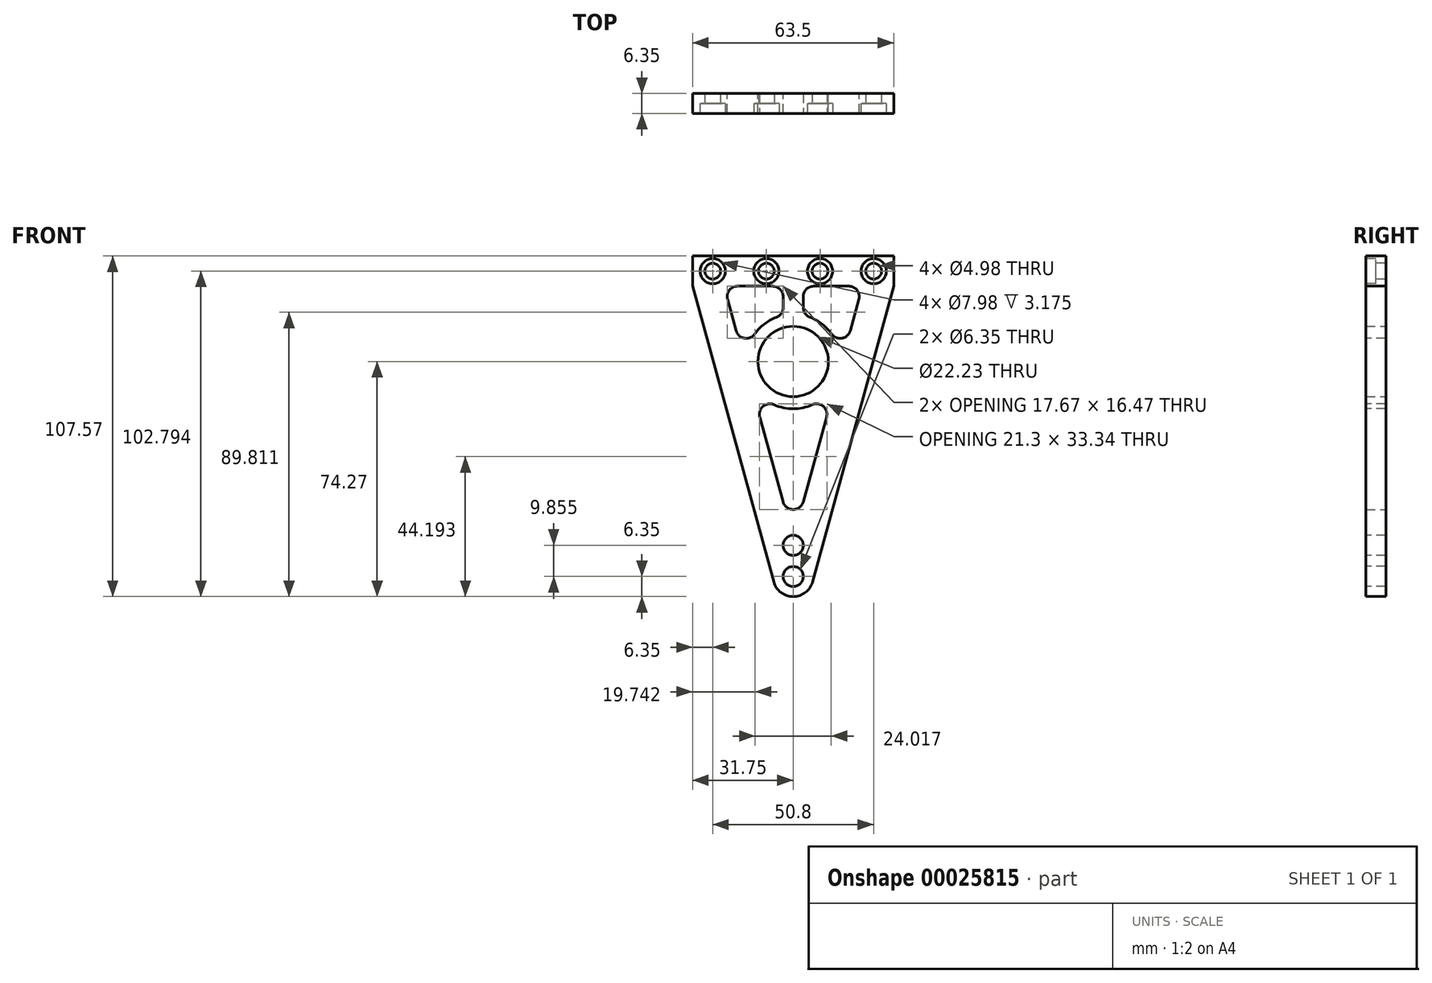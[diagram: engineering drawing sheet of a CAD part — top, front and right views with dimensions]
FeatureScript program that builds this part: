
annotation { "Feature Type Name" : "Feature", "Feature Type Description" : "" }
export const myFeature = defineFeature(function(context is Context, id is Id, definition is map)
    precondition{}
    {
        {
            var Q0;
            Q0=qCreatedBy(makeId("Front.planeOp"),FACE);
            var sketch = newSketch(context, id + "F0", { "sketchPlane" : qUnion([Q0])});
            skCircle(sketch, "E0", {"center": v(0, 0) * mm, "radius": 11.11 * mm});
            skLineSegment(sketch, "E1", {"start": v(0, 0) * mm, "end": v(0, 46.7) * mm, "construction": true});
            skLineSegment(sketch, "E2", {"start": v(0, 0) * mm, "end": v(31.75, 0) * mm, "construction": true});
            skLineSegment(sketch, "E3", {"start": v(-31.75, 33.3) * mm, "end": v(31.75, 33.3) * mm});
            skLineSegment(sketch, "E4", {"start": v(31.75, 33.3) * mm, "end": v(31.75, 23.77) * mm});
            skLineSegment(sketch, "E5", {"start": v(31.75, 23.77) * mm, "end": v(6.12, -69.6) * mm});
            skLineSegment(sketch, "E6", {"start": v(-6.12, -69.6) * mm, "end": v(-31.75, 23.77) * mm});
            skLineSegment(sketch, "E7", {"start": v(-31.75, 23.77) * mm, "end": v(-31.75, 33.3) * mm});
            skArc(sketch, "E8", {"start": v(-6.12, -69.6) * mm, "mid": v(0, -74.27) * mm, "end": v(6.12, -69.6) * mm});
            skSolve(sketch);
        }
        {
            var Q0;
            Q0=makeQuery(id+"F0.imprint","IMPRINT",FACE,{"disambiguationData":[TD([[makeQuery(id+"F0.imprint","IMPRINT",EDGE,{"derivedFrom":sQuery(id+"F0.wireOp",EDGE,"E0")}),-1.0]])]});
            extrude(context, id + "F1", {"entities" : qUnion([Q0]), "depth" : 6.35 * mm});
        }
        {
            var Q0;
            Q0=makeQuery(id+"F1.opExtrude","CAP_FACE",FACE,{"disambiguationData":[OSD([sQuery(id+"F0.wireOp",EDGE,"E0"),sQuery(id+"F0.wireOp",EDGE,"E3"),sQuery(id+"F0.wireOp",EDGE,"E4"),sQuery(id+"F0.wireOp",EDGE,"E5"),sQuery(id+"F0.wireOp",EDGE,"E6"),sQuery(id+"F0.wireOp",EDGE,"E7"),sQuery(id+"F0.wireOp",EDGE,"E8")])],"isStart":false});
            var sketch = newSketch(context, id + "F2", { "sketchPlane" : qUnion([Q0])});
            skLineSegment(sketch, "E9.0", {"start": v(21.87, 23.77) * mm, "end": v(3.17, 23.77) * mm});
            skLineSegment(sketch, "E9.1", {"start": v(0, -55.92) * mm, "end": v(13.77, -5.75) * mm});
            skLineSegment(sketch, "E9.2", {"start": v(-21.87, 23.77) * mm, "end": v(-14.78, -2.08) * mm});
            skArc(sketch, "E10", {"start": v(-13.77, -5.75) * mm, "mid": v(0, -14.92) * mm, "end": v(13.77, -5.75) * mm});
            skArc(sketch, "E11.trimOffspring", {"start": v(14.78, -2.08) * mm, "mid": v(12.25, 8.53) * mm, "end": v(3.18, 14.58) * mm});
            skLineSegment(sketch, "E12.trimOffspring", {"start": v(14.78, -2.08) * mm, "end": v(21.87, 23.77) * mm});
            skLineSegment(sketch, "E13.trimOffspring", {"start": v(-13.77, -5.75) * mm, "end": v(0, -55.92) * mm});
            skLineSegment(sketch, "E14", {"start": v(0, 0) * mm, "end": v(0, 36.66) * mm, "construction": true});
            skLineSegment(sketch, "E15", {"start": v(-3.17, 23.77) * mm, "end": v(-3.18, 14.58) * mm});
            skLineSegment(sketch, "E16", {"start": v(3.17, 23.77) * mm, "end": v(3.18, 14.58) * mm});
            skPoint(sketch, "E17.orphan", {"position": v(3.18, 0) * mm});
            skPoint(sketch, "E18.orphan", {"position": v(-3.18, 0) * mm});
            skArc(sketch, "E19.trimOffspring", {"start": v(-3.18, 14.58) * mm, "mid": v(-12.25, 8.53) * mm, "end": v(-14.78, -2.08) * mm});
            skLineSegment(sketch, "E20.trimOffspring", {"start": v(-3.17, 23.77) * mm, "end": v(-21.87, 23.77) * mm});
            skSolve(sketch);
        }
        {
            var Q0;
            Q0=makeQuery(id+"F2.imprint","IMPRINT",FACE,{"disambiguationData":[TD([[makeQuery(id+"F2.imprint","IMPRINT",EDGE,{"derivedFrom":sQuery(id+"F2.wireOp",EDGE,"E9.2")}),1.0]])]});
            var Q1;
            Q1=makeQuery(id+"F2.imprint","IMPRINT",FACE,{"disambiguationData":[TD([[makeQuery(id+"F2.imprint","IMPRINT",EDGE,{"derivedFrom":sQuery(id+"F2.wireOp",EDGE,"E9.0")}),1.0]])]});
            var Q2;
            Q2=makeQuery(id+"F2.imprint","IMPRINT",FACE,{"disambiguationData":[TD([[makeQuery(id+"F2.imprint","IMPRINT",EDGE,{"derivedFrom":sQuery(id+"F2.wireOp",EDGE,"E9.1")}),1.0]])]});
            extrude(context, id + "F3", {"entities" : qUnion([Q0, Q1, Q2]), "operationType" : NewBodyOperationType.REMOVE, "endBound" : BoundingType.THROUGH_ALL, "oppositeDirection" : true, "depth" : 25.4 * mm});
        }
        {
            var Q0;
            Q0=makeQuery(id+"F3.boolean.opBoolean","COPY",EDGE,{"derivedFrom":makeQuery(id+"F3.opExtrude","SWEPT_EDGE",EDGE,{"disambiguationData":[OSD([sQuery(id+"F2.wireOp",EDGE,"E9.0"),sQuery(id+"F2.wireOp",EDGE,"E12.trimOffspring")])]})});
            var Q1;
            Q1=makeQuery(id+"F3.boolean.opBoolean","COPY",EDGE,{"derivedFrom":makeQuery(id+"F3.opExtrude","SWEPT_EDGE",EDGE,{"disambiguationData":[OSD([sQuery(id+"F2.wireOp",EDGE,"E15"),sQuery(id+"F2.wireOp",EDGE,"E20.trimOffspring")])]})});
            var Q2;
            Q2=makeQuery(id+"F3.boolean.opBoolean","COPY",EDGE,{"derivedFrom":makeQuery(id+"F3.opExtrude","SWEPT_EDGE",EDGE,{"disambiguationData":[OSD([sQuery(id+"F2.wireOp",EDGE,"E9.0"),sQuery(id+"F2.wireOp",EDGE,"E16")])]})});
            var Q3;
            Q3=makeQuery(id+"F3.boolean.opBoolean","COPY",EDGE,{"derivedFrom":makeQuery(id+"F3.opExtrude","SWEPT_EDGE",EDGE,{"disambiguationData":[OSD([sQuery(id+"F2.wireOp",EDGE,"E9.2"),sQuery(id+"F2.wireOp",EDGE,"E20.trimOffspring")])]})});
            var Q4;
            Q4=makeQuery(id+"F3.boolean.opBoolean","COPY",EDGE,{"derivedFrom":makeQuery(id+"F3.opExtrude","SWEPT_EDGE",EDGE,{"disambiguationData":[OSD([sQuery(id+"F2.wireOp",EDGE,"E11.trimOffspring"),sQuery(id+"F2.wireOp",EDGE,"E12.trimOffspring")])]})});
            var Q5;
            Q5=makeQuery(id+"F3.boolean.opBoolean","COPY",EDGE,{"derivedFrom":makeQuery(id+"F3.opExtrude","SWEPT_EDGE",EDGE,{"disambiguationData":[OSD([sQuery(id+"F2.wireOp",EDGE,"E9.2"),sQuery(id+"F2.wireOp",EDGE,"E19.trimOffspring")])]})});
            var Q6;
            Q6=makeQuery(id+"F3.boolean.opBoolean","COPY",EDGE,{"derivedFrom":makeQuery(id+"F3.opExtrude","SWEPT_EDGE",EDGE,{"disambiguationData":[OSD([sQuery(id+"F2.wireOp",EDGE,"E9.1"),sQuery(id+"F2.wireOp",EDGE,"E13.trimOffspring")])]})});
            var Q7;
            Q7=makeQuery(id+"F3.boolean.opBoolean","COPY",EDGE,{"derivedFrom":makeQuery(id+"F3.opExtrude","SWEPT_EDGE",EDGE,{"disambiguationData":[OSD([sQuery(id+"F2.wireOp",EDGE,"E10"),sQuery(id+"F2.wireOp",EDGE,"E13.trimOffspring")])]})});
            var Q8;
            Q8=makeQuery(id+"F3.boolean.opBoolean","COPY",EDGE,{"derivedFrom":makeQuery(id+"F3.opExtrude","SWEPT_EDGE",EDGE,{"disambiguationData":[OSD([sQuery(id+"F2.wireOp",EDGE,"E9.1"),sQuery(id+"F2.wireOp",EDGE,"E10")])]})});
            var Q9;
            Q9=makeQuery(id+"F3.boolean.opBoolean","COPY",EDGE,{"derivedFrom":makeQuery(id+"F3.opExtrude","SWEPT_EDGE",EDGE,{"disambiguationData":[OSD([sQuery(id+"F2.wireOp",EDGE,"E11.trimOffspring"),sQuery(id+"F2.wireOp",EDGE,"E16")])]})});
            var Q10;
            Q10=makeQuery(id+"F3.boolean.opBoolean","COPY",EDGE,{"derivedFrom":makeQuery(id+"F3.opExtrude","SWEPT_EDGE",EDGE,{"disambiguationData":[OSD([sQuery(id+"F2.wireOp",EDGE,"E15"),sQuery(id+"F2.wireOp",EDGE,"E19.trimOffspring")])]})});
            fillet(context, id + "F4", {"entities" : qUnion([Q0, Q1, Q2, Q3, Q4, Q5, Q6, Q7, Q8, Q9, Q10]), "radius" : 3.3 * mm, "tangentPropagation" : true, "allowEdgeOverflow" : false});
        }
        {
            var Q0;
            Q0=makeQuery(id+"F1.opExtrude","CAP_FACE",FACE,{"disambiguationData":[OSD([sQuery(id+"F0.wireOp",EDGE,"E0"),sQuery(id+"F0.wireOp",EDGE,"E3"),sQuery(id+"F0.wireOp",EDGE,"E4"),sQuery(id+"F0.wireOp",EDGE,"E5"),sQuery(id+"F0.wireOp",EDGE,"E6"),sQuery(id+"F0.wireOp",EDGE,"E7"),sQuery(id+"F0.wireOp",EDGE,"E8")])],"isStart":false});
            var sketch = newSketch(context, id + "F5", { "sketchPlane" : qUnion([Q0])});
            skLineSegment(sketch, "E21", {"start": v(-25.4, 28.52) * mm, "end": v(25.4, 28.52) * mm});
            skLineSegment(sketch, "E22", {"start": v(25.4, 28.52) * mm, "end": v(0, 28.52) * mm});
            skLineSegment(sketch, "E23", {"start": v(0, 28.52) * mm, "end": v(0, -67.92) * mm});
            skPoint(sketch, "E24", {"position": v(-8.47, 28.52) * mm});
            skPoint(sketch, "E25", {"position": v(8.47, 28.52) * mm});
            skPoint(sketch, "E26", {"position": v(0, -58.06) * mm});
            skPoint(sketch, "E27", {"position": v(-25.4, 28.52) * mm});
            skPoint(sketch, "E28", {"position": v(25.4, 28.52) * mm});
            skSolve(sketch);
        }
        {
            var Q0;
            Q0=sQuery(id+"F5.wireOp",VERTEX,"E27");
            var Q1;
            Q1=sQuery(id+"F5.wireOp",VERTEX,"E24");
            var Q2;
            Q2=sQuery(id+"F5.wireOp",VERTEX,"E25");
            var Q3;
            Q3=sQuery(id+"F5.wireOp",VERTEX,"E28");
            var Q4;
            Q4=makeQuery(id+"F1.opExtrude","SWEPT_BODY",BODY,{"disambiguationData":[OSD([sQuery(id+"F0.wireOp",EDGE,"E0"),sQuery(id+"F0.wireOp",EDGE,"E3"),sQuery(id+"F0.wireOp",EDGE,"E4"),sQuery(id+"F0.wireOp",EDGE,"E5"),sQuery(id+"F0.wireOp",EDGE,"E6"),sQuery(id+"F0.wireOp",EDGE,"E7"),sQuery(id+"F0.wireOp",EDGE,"E8")])]});
            hole(context, id + "F6", {"style" : HoleStyle.C_BORE, "holeDiameter" : 4.98 * mm, "cBoreDiameter" : 7.98 * mm, "cBoreDepth" : 3.17 * mm, "endStyle" : HoleEndStyle.THROUGH, "locations" : qUnion([Q0, Q1, Q2, Q3]), "scope" : qUnion([Q4])});
        }
        {
            var Q0;
            Q0=sQuery(id+"F5.wireOp",VERTEX,"E26");
            var Q1;
            Q1=sQuery(id+"F5.wireOp",VERTEX,"E23.end");
            var Q2;
            Q2=makeQuery(id+"F1.opExtrude","SWEPT_BODY",BODY,{"disambiguationData":[OSD([sQuery(id+"F0.wireOp",EDGE,"E0"),sQuery(id+"F0.wireOp",EDGE,"E3"),sQuery(id+"F0.wireOp",EDGE,"E4"),sQuery(id+"F0.wireOp",EDGE,"E5"),sQuery(id+"F0.wireOp",EDGE,"E6"),sQuery(id+"F0.wireOp",EDGE,"E7"),sQuery(id+"F0.wireOp",EDGE,"E8")])]});
            hole(context, id + "F7", {"style" : HoleStyle.SIMPLE, "holeDiameter" : 6.35 * mm, "endStyle" : HoleEndStyle.THROUGH, "locations" : qUnion([Q0, Q1]), "scope" : qUnion([Q2])});
        }
    });
